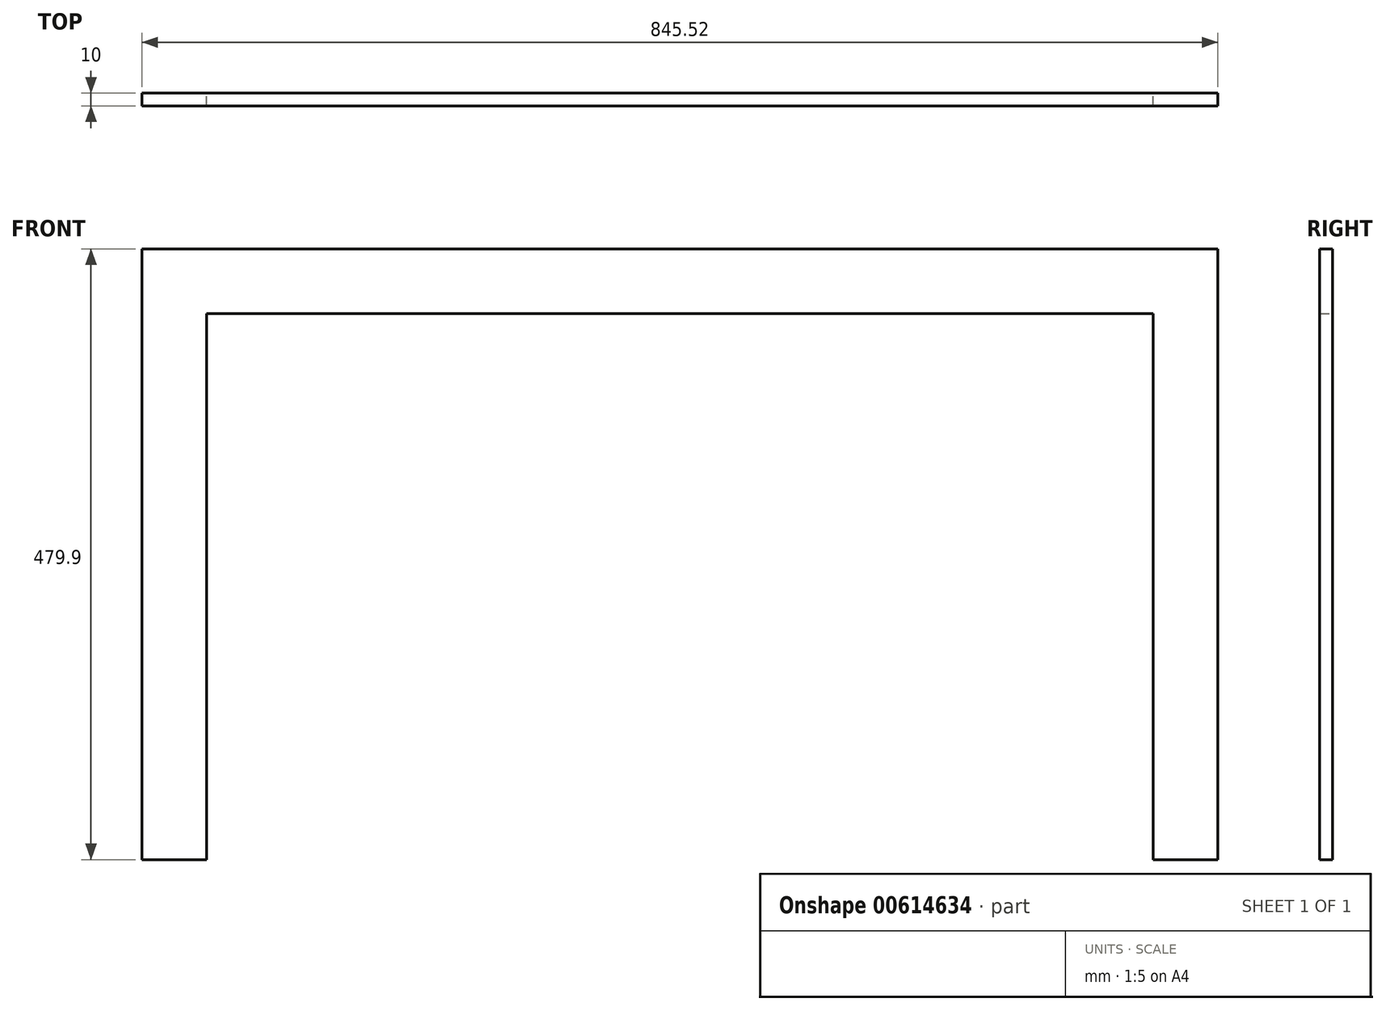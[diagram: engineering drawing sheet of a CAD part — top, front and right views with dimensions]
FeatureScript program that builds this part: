
annotation { "Feature Type Name" : "Feature", "Feature Type Description" : "" }
export const myFeature = defineFeature(function(context is Context, id is Id, definition is map)
    precondition{}
    {
        {
            var Q0;
            Q0=qCreatedBy(makeId("Front.planeOp"),FACE);
            var sketch = newSketch(context, id + "F0", { "sketchPlane" : qUnion([Q0])});
            skLineSegment(sketch, "E0.bottom", {"start": v(422.76, -239.95) * mm, "end": v(-422.76, -239.95) * mm});
            skLineSegment(sketch, "E0.top", {"start": v(422.76, 239.95) * mm, "end": v(-422.76, 239.95) * mm});
            skLineSegment(sketch, "E0.left", {"start": v(422.76, -239.95) * mm, "end": v(422.76, 239.95) * mm});
            skLineSegment(sketch, "E0.right", {"start": v(-422.76, -239.95) * mm, "end": v(-422.76, 239.95) * mm});
            skPoint(sketch, "E0.middle", {"position": v(0, 0) * mm});
            skSolve(sketch);
        }
        {
            var Q0;
            Q0=makeQuery(id+"F0.imprint","IMPRINT",FACE,{"disambiguationData":[TD([[makeQuery(id+"F0.imprint","IMPRINT",EDGE,{"derivedFrom":sQuery(id+"F0.wireOp",EDGE,"E0.bottom")}),-1.0]])]});
            extrude(context, id + "F1", {"entities" : qUnion([Q0]), "depth" : 10 * mm});
        }
        {
            var Q0;
            Q0=makeQuery(id+"F1.opExtrude","CAP_FACE",FACE,{"disambiguationData":[OSD([sQuery(id+"F0.wireOp",EDGE,"E0.bottom"),sQuery(id+"F0.wireOp",EDGE,"E0.top"),sQuery(id+"F0.wireOp",EDGE,"E0.left"),sQuery(id+"F0.wireOp",EDGE,"E0.right")])],"isStart":true});
            var sketch = newSketch(context, id + "F2", { "sketchPlane" : qUnion([Q0])});
            skLineSegment(sketch, "E1.bottom", {"start": v(-371.96, 189.15) * mm, "end": v(371.96, 189.15) * mm});
            skLineSegment(sketch, "E1.top", {"start": v(-371.96, -239.95) * mm, "end": v(371.96, -239.95) * mm});
            skLineSegment(sketch, "E1.left", {"start": v(-371.96, 189.15) * mm, "end": v(-371.96, -239.95) * mm});
            skLineSegment(sketch, "E1.right", {"start": v(371.96, 189.15) * mm, "end": v(371.96, -239.95) * mm});
            skSolve(sketch);
        }
        {
            var Q0;
            Q0=makeQuery(id+"F2.imprint","IMPRINT",FACE,{"disambiguationData":[TD([[makeQuery(id+"F2.imprint","IMPRINT",EDGE,{"derivedFrom":sQuery(id+"F2.wireOp",EDGE,"E1.bottom")}),-1.0]])]});
            extrude(context, id + "F3", {"entities" : qUnion([Q0]), "operationType" : NewBodyOperationType.REMOVE, "endBound" : BoundingType.THROUGH_ALL, "oppositeDirection" : true, "depth" : 25.4 * mm, "offsetDistance" : 25.4 * mm});
        }
    });
